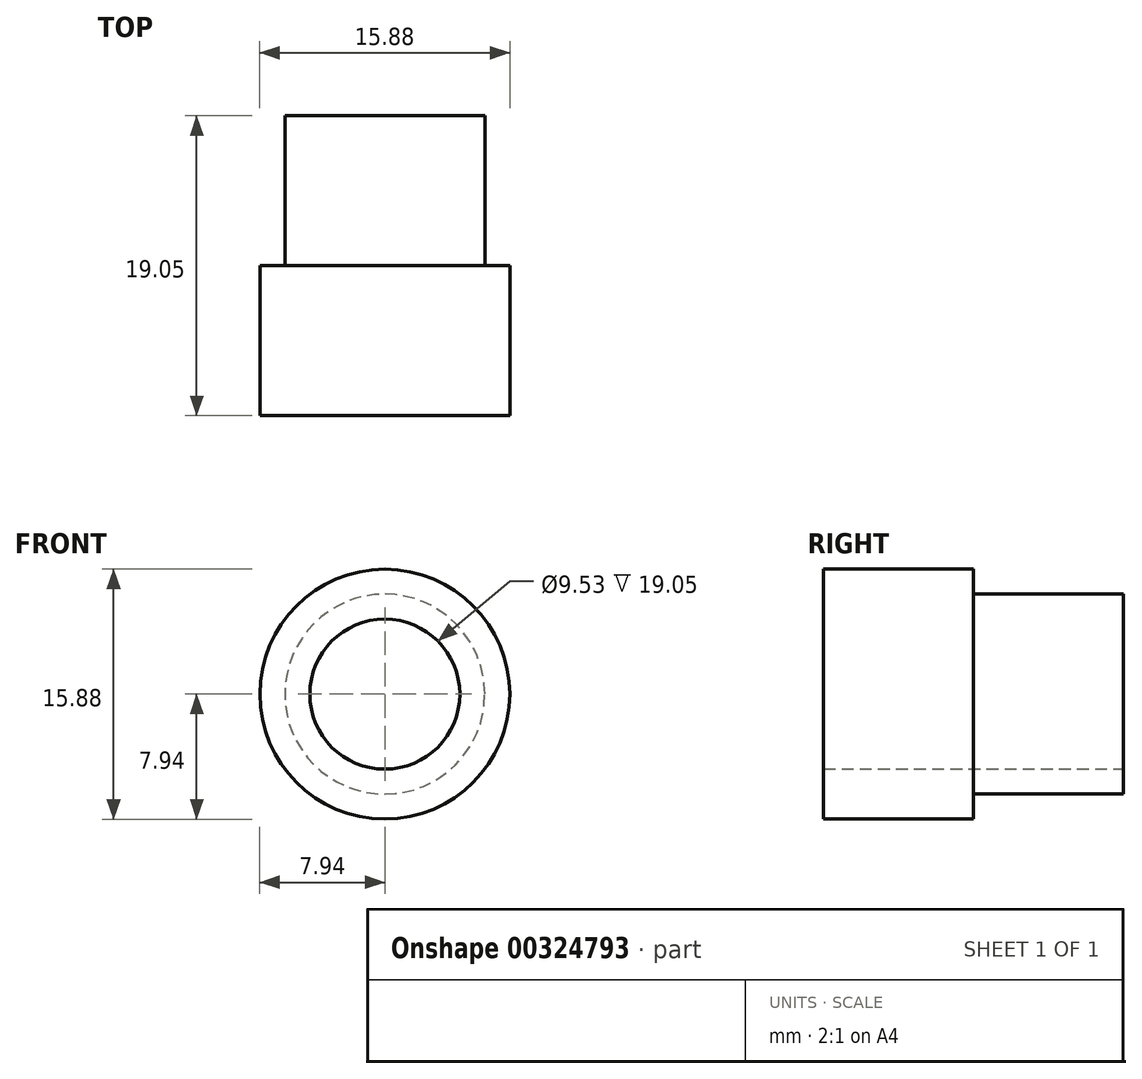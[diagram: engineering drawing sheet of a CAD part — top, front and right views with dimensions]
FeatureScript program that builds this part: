
annotation { "Feature Type Name" : "Feature", "Feature Type Description" : "" }
export const myFeature = defineFeature(function(context is Context, id is Id, definition is map)
    precondition{}
    {
        {
            var Q0;
            Q0=qCreatedBy(makeId("Front.planeOp"),FACE);
            var sketch = newSketch(context, id + "F0", { "sketchPlane" : qUnion([Q0])});
            skCircle(sketch, "E0", {"center": v(0, 0) * mm, "radius": 4.76 * mm});
            skCircle(sketch, "E1", {"center": v(0, 0) * mm, "radius": 6.35 * mm});
            skSolve(sketch);
        }
        {
            var Q0;
            Q0=makeQuery(id+"F0.imprint","IMPRINT",FACE,{"disambiguationData":[TD([[makeQuery(id+"F0.imprint","IMPRINT",EDGE,{"derivedFrom":sQuery(id+"F0.wireOp",EDGE,"E0")}),-1.0]])]});
            extrude(context, id + "F1", {"entities" : qUnion([Q0]), "depth" : 9.52 * mm, "offsetDistance" : 25.4 * mm});
        }
        {
            var Q0;
            Q0=makeQuery(id+"F1.opExtrude","CAP_FACE",FACE,{"disambiguationData":[OSD([sQuery(id+"F0.wireOp",EDGE,"E0"),sQuery(id+"F0.wireOp",EDGE,"E1")])],"isStart":false});
            var sketch = newSketch(context, id + "F2", { "sketchPlane" : qUnion([Q0])});
            skCircle(sketch, "E2", {"center": v(0, 0) * mm, "radius": 4.76 * mm});
            skCircle(sketch, "E3", {"center": v(0, 0) * mm, "radius": 7.94 * mm});
            skSolve(sketch);
        }
        {
            var Q0;
            Q0=makeQuery(id+"F2.imprint","IMPRINT",FACE,{"disambiguationData":[TD([[makeQuery(id+"F2.imprint","IMPRINT",EDGE,{"derivedFrom":sQuery(id+"F2.wireOp",EDGE,"E3")}),1.0]])]});
            var Q1;
            Q1=makeQuery(id+"F2.imprint","IMPRINT",FACE,{"disambiguationData":[TD([[makeQuery(id+"F2.imprint","IMPRINT",EDGE,{"derivedFrom":sQuery(id+"F2.wireOp",EDGE,"E2")}),-1.0]])]});
            extrude(context, id + "F3", {"entities" : qUnion([Q0, Q1]), "operationType" : NewBodyOperationType.ADD, "depth" : 9.52 * mm, "offsetDistance" : 25.4 * mm});
        }
    });
